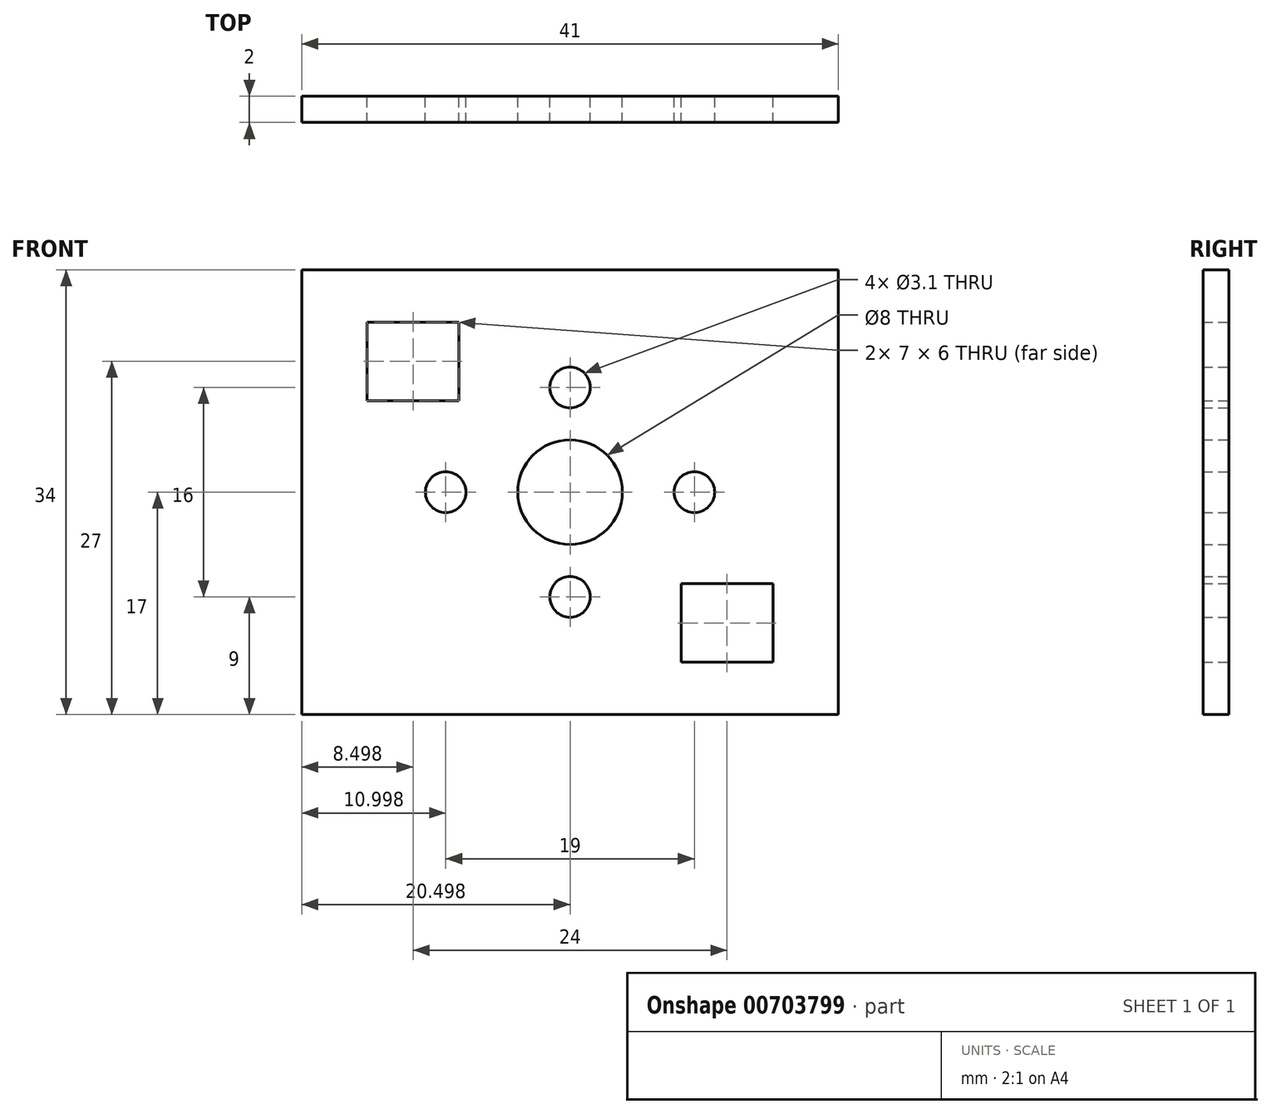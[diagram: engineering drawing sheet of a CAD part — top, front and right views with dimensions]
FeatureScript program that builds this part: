
annotation { "Feature Type Name" : "Feature", "Feature Type Description" : "" }
export const myFeature = defineFeature(function(context is Context, id is Id, definition is map)
    precondition{}
    {
        {
            var Q0;
            Q0=qCreatedBy(makeId("Top.planeOp"),FACE);
            var sketch = newSketch(context, id + "F0", { "sketchPlane" : qUnion([Q0])});
            skLineSegment(sketch, "E0.bottom", {"start": v(-22.2, 49.2) * mm, "end": v(18.8, 49.2) * mm});
            skLineSegment(sketch, "E0.top", {"start": v(-22.2, -40.8) * mm, "end": v(18.8, -40.8) * mm});
            skLineSegment(sketch, "E0.left", {"start": v(-22.2, 49.2) * mm, "end": v(-22.2, -40.8) * mm});
            skLineSegment(sketch, "E0.right", {"start": v(18.8, 49.2) * mm, "end": v(18.8, -40.8) * mm});
            skSolve(sketch);
        }
        {
            var Q0;
            Q0=makeQuery(id+"F0.imprint","IMPRINT",FACE,{"disambiguationData":[TD([[makeQuery(id+"F0.imprint","IMPRINT",EDGE,{"derivedFrom":sQuery(id+"F0.wireOp",EDGE,"E0.bottom")}),-1.0]])]});
            extrude(context, id + "F1", {"entities" : qUnion([Q0]), "depth" : 34 * mm, "offsetDistance" : 25 * mm});
        }
        {
            var Q0;
            Q0=makeQuery(id+"F1.opExtrude","SWEPT_FACE",FACE,{"disambiguationData":[OSD([sQuery(id+"F0.wireOp",EDGE,"E0.top")])]});
            var sketch = newSketch(context, id + "F2", { "sketchPlane" : qUnion([Q0])});
            skLineSegment(sketch, "E1.bottom", {"start": v(-19.2, 31.5) * mm, "end": v(15.8, 31.5) * mm});
            skLineSegment(sketch, "E1.top", {"start": v(-19.2, 2.5) * mm, "end": v(15.8, 2.5) * mm});
            skLineSegment(sketch, "E1.left", {"start": v(-19.2, 31.5) * mm, "end": v(-19.2, 2.5) * mm});
            skLineSegment(sketch, "E1.right", {"start": v(15.8, 31.5) * mm, "end": v(15.8, 2.5) * mm});
            skSolve(sketch);
        }
        {
            var Q0;
            Q0=makeQuery(id+"F2.imprint","IMPRINT",FACE,{"disambiguationData":[TD([[makeQuery(id+"F2.imprint","IMPRINT",EDGE,{"derivedFrom":sQuery(id+"F2.wireOp",EDGE,"E1.bottom")}),-1.0]])]});
            extrude(context, id + "F3", {"entities" : qUnion([Q0]), "operationType" : NewBodyOperationType.REMOVE, "oppositeDirection" : true, "depth" : 86 * mm, "offsetDistance" : 25 * mm});
        }
        {
            var Q0;
            Q0=makeQuery(id+"F1.opExtrude","SWEPT_FACE",FACE,{"disambiguationData":[OSD([sQuery(id+"F0.wireOp",EDGE,"E0.bottom")])]});
            var sketch = newSketch(context, id + "F4", { "sketchPlane" : qUnion([Q0])});
            skCircle(sketch, "E2", {"center": v(1.7, 17) * mm, "radius": 4 * mm});
            skCircle(sketch, "E3", {"center": v(-7.8, 17) * mm, "radius": 1.55 * mm});
            skCircle(sketch, "E4", {"center": v(11.2, 17) * mm, "radius": 1.55 * mm});
            skLineSegment(sketch, "E5.bottom", {"start": v(10.2, 30) * mm, "end": v(17.2, 30) * mm});
            skLineSegment(sketch, "E5.top", {"start": v(10.2, 24) * mm, "end": v(17.2, 24) * mm});
            skLineSegment(sketch, "E5.left", {"start": v(10.2, 30) * mm, "end": v(10.2, 24) * mm});
            skLineSegment(sketch, "E5.right", {"start": v(17.2, 30) * mm, "end": v(17.2, 24) * mm});
            skLineSegment(sketch, "E6.bottom", {"start": v(-13.8, 10) * mm, "end": v(-6.8, 10) * mm});
            skLineSegment(sketch, "E6.top", {"start": v(-13.8, 4) * mm, "end": v(-6.8, 4) * mm});
            skLineSegment(sketch, "E6.left", {"start": v(-13.8, 10) * mm, "end": v(-13.8, 4) * mm});
            skLineSegment(sketch, "E6.right", {"start": v(-6.8, 10) * mm, "end": v(-6.8, 4) * mm});
            skCircle(sketch, "E7", {"center": v(1.7, 9) * mm, "radius": 1.55 * mm});
            skCircle(sketch, "E8", {"center": v(1.7, 25) * mm, "radius": 1.55 * mm});
            skSolve(sketch);
        }
        {
            var Q0;
            Q0=makeQuery(id+"F4.imprint","IMPRINT",FACE,{"disambiguationData":[TD([[makeQuery(id+"F4.imprint","IMPRINT",EDGE,{"derivedFrom":sQuery(id+"F4.wireOp",EDGE,"E6.bottom")}),-1.0]])]});
            var Q1;
            Q1=makeQuery(id+"F4.imprint","IMPRINT",FACE,{"disambiguationData":[TD([[makeQuery(id+"F4.imprint","IMPRINT",EDGE,{"derivedFrom":sQuery(id+"F4.wireOp",EDGE,"E2")}),1.0]])]});
            var Q2;
            Q2=makeQuery(id+"F4.imprint","IMPRINT",FACE,{"disambiguationData":[TD([[makeQuery(id+"F4.imprint","IMPRINT",EDGE,{"derivedFrom":sQuery(id+"F4.wireOp",EDGE,"E5.bottom")}),-1.0]])]});
            var Q3;
            Q3=makeQuery(id+"F4.imprint","IMPRINT",FACE,{"disambiguationData":[TD([[makeQuery(id+"F4.imprint","IMPRINT",EDGE,{"derivedFrom":sQuery(id+"F4.wireOp",EDGE,"E4")}),1.0]])]});
            var Q4;
            Q4=makeQuery(id+"F4.imprint","IMPRINT",FACE,{"disambiguationData":[TD([[makeQuery(id+"F4.imprint","IMPRINT",EDGE,{"derivedFrom":sQuery(id+"F4.wireOp",EDGE,"E3")}),1.0]])]});
            var Q5;
            Q5=makeQuery(id+"F4.imprint","IMPRINT",FACE,{"disambiguationData":[TD([[makeQuery(id+"F4.imprint","IMPRINT",EDGE,{"derivedFrom":sQuery(id+"F4.wireOp",EDGE,"E8")}),1.0]])]});
            var Q6;
            Q6=makeQuery(id+"F4.imprint","IMPRINT",FACE,{"disambiguationData":[TD([[makeQuery(id+"F4.imprint","IMPRINT",EDGE,{"derivedFrom":sQuery(id+"F4.wireOp",EDGE,"E7")}),1.0]])]});
            extrude(context, id + "F5", {"entities" : qUnion([Q0, Q1, Q2, Q3, Q4, Q5, Q6]), "operationType" : NewBodyOperationType.REMOVE, "endBound" : BoundingType.UP_TO_NEXT, "oppositeDirection" : true, "depth" : 25 * mm, "offsetDistance" : 25 * mm});
        }
        {
            var Q0;
            Q0=makeQuery(id+"F1.opExtrude","SWEPT_FACE",FACE,{"disambiguationData":[OSD([sQuery(id+"F0.wireOp",EDGE,"E0.top")])]});
            extrude(context, id + "F6", {"entities" : qUnion([Q0]), "operationType" : NewBodyOperationType.REMOVE, "oppositeDirection" : true, "depth" : 86 * mm, "offsetDistance" : 25 * mm});
        }
        {
            var Q0;
            Q0=makeQuery(id+"F6.boolean.opBoolean","MERGE",FACE,{"derivedFrom":[makeQuery(id+"F3.boolean.opBoolean","COPY",FACE,{"derivedFrom":makeQuery(id+"F3.opExtrude","CAP_FACE",FACE,{"disambiguationData":[OSD([sQuery(id+"F2.wireOp",EDGE,"E1.bottom"),sQuery(id+"F2.wireOp",EDGE,"E1.top"),sQuery(id+"F2.wireOp",EDGE,"E1.left"),sQuery(id+"F2.wireOp",EDGE,"E1.right")])],"isStart":false})}),makeQuery(id+"F6.opExtrude","CAP_FACE",FACE,{"disambiguationData":[OSD([sQuery(id+"F0.wireOp",EDGE,"E0.top")])],"isStart":false})]});
            extrude(context, id + "F7", {"entities" : qUnion([Q0]), "operationType" : NewBodyOperationType.REMOVE, "oppositeDirection" : true, "depth" : 2 * mm, "offsetDistance" : 25 * mm});
        }
    });
